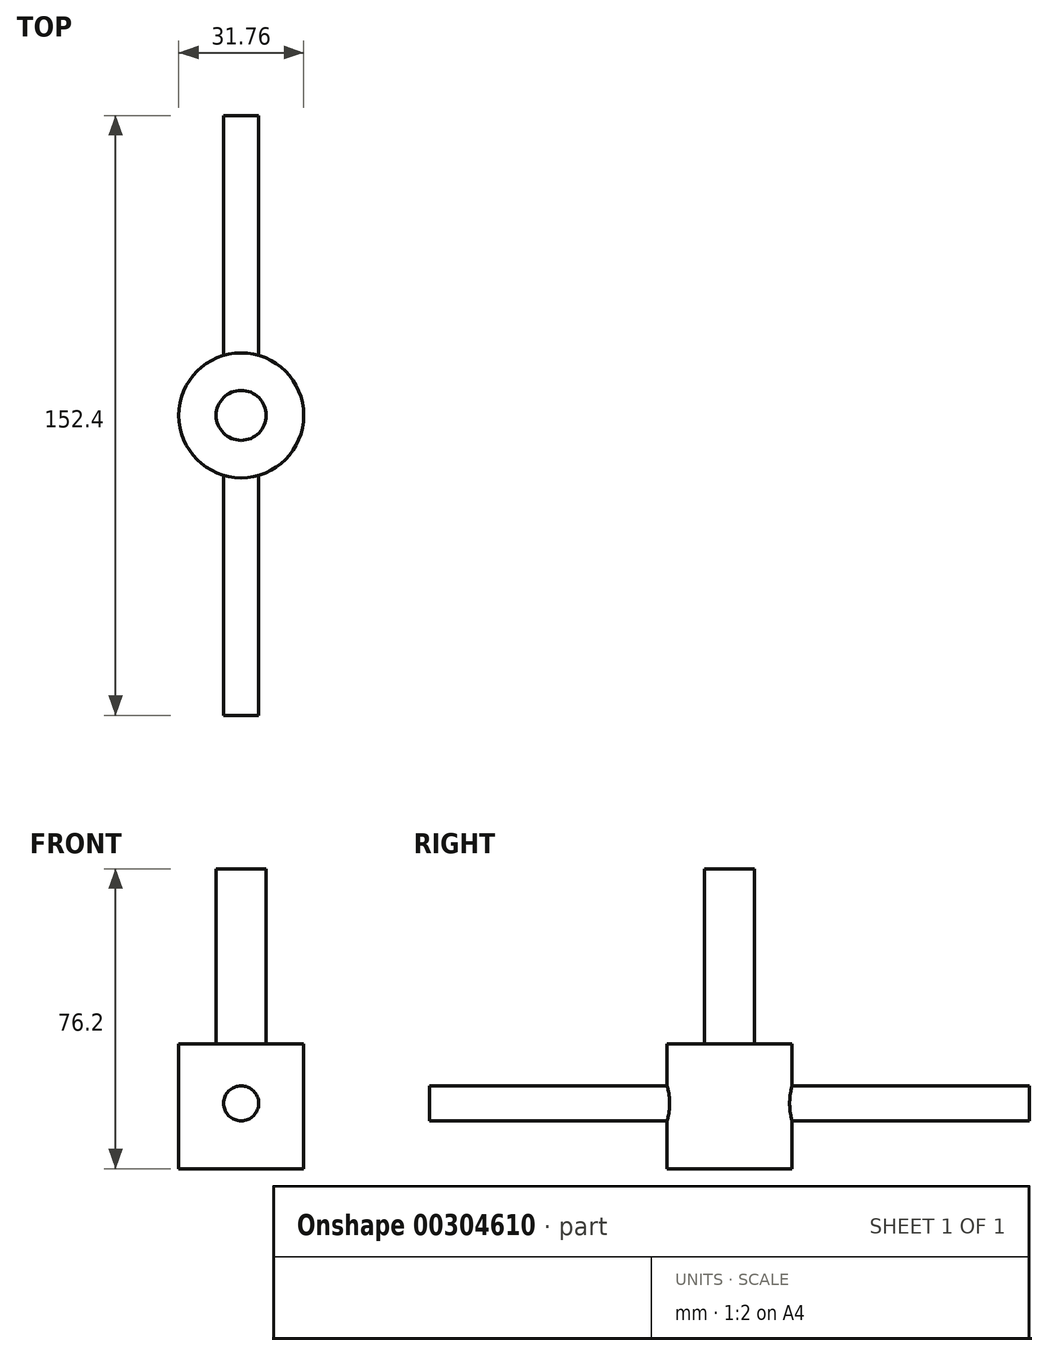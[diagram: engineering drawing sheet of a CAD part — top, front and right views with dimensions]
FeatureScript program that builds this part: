
annotation { "Feature Type Name" : "Feature", "Feature Type Description" : "" }
export const myFeature = defineFeature(function(context is Context, id is Id, definition is map)
    precondition{}
    {
        {
            var Q0;
            Q0=qCreatedBy(makeId("Top.planeOp"),FACE);
            var sketch = newSketch(context, id + "F0", { "sketchPlane" : qUnion([Q0])});
            skCircle(sketch, "E0", {"center": v(0, 0) * mm, "radius": 15.88 * mm});
            skSolve(sketch);
        }
        {
            var Q0;
            Q0 = qSketchRegion(id + "F0", true);
            extrude(context, id + "F1", {"entities" : qUnion([Q0]), "depth" : 31.75 * mm});
        }
        {
            var Q0;
            Q0=makeQuery(id+"F1.opExtrude","CAP_FACE",FACE,{"disambiguationData":[OSD([sQuery(id+"F0.wireOp",EDGE,"E0")])],"isStart":false});
            var sketch = newSketch(context, id + "F2", { "sketchPlane" : qUnion([Q0])});
            skCircle(sketch, "E1", {"center": v(0, 0) * mm, "radius": 6.35 * mm});
            skSolve(sketch);
        }
        {
            var Q0;
            Q0 = qSketchRegion(id + "F2", true);
            extrude(context, id + "F3", {"entities" : qUnion([Q0]), "operationType" : NewBodyOperationType.ADD, "depth" : 44.45 * mm});
        }
        {
            var Q0;
            Q0=qCreatedBy(makeId("Front.planeOp"),FACE);
            var sketch = newSketch(context, id + "F4", { "sketchPlane" : qUnion([Q0])});
            skCircle(sketch, "E2", {"center": v(0, 16.6) * mm, "radius": 4.45 * mm});
            skSolve(sketch);
        }
        {
            var Q0;
            Q0 = qSketchRegion(id + "F4", true);
            extrude(context, id + "F5", {"entities" : qUnion([Q0]), "operationType" : NewBodyOperationType.ADD, "endBound" : BoundingType.SYMMETRIC, "depth" : 152.4 * mm});
        }
        {
            var Q0;
            Q0=qCreatedBy(makeId("Front.planeOp"),FACE);
            cPlane(context, id + "F6", {"entities" : qUnion([Q0]), "cplaneType" : CPlaneType.OFFSET, "offset" : 76.2 * mm, "width" : 152.4 * mm, "height" : 152.4 * mm});
        }
    });
